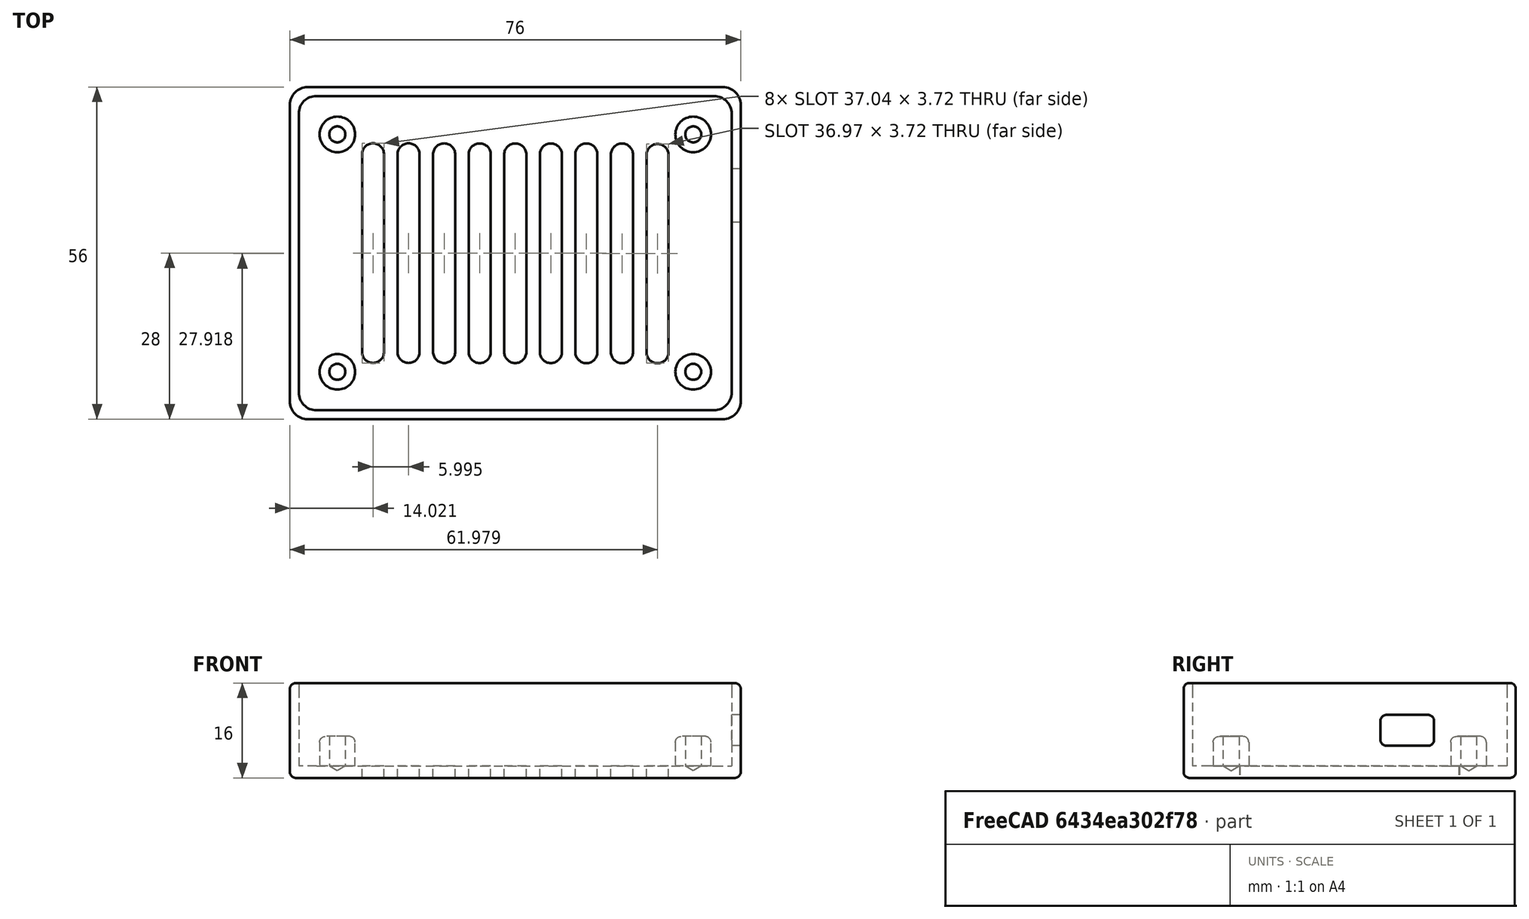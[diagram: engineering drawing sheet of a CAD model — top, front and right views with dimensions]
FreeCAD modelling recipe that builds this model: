
FCSTD DOCUMENT  (FreeCAD 0.19R24267 +99 (Git))
Label: shell_nixie_clock_lite
License: All rights reserved
LicenseURL: http://en.wikipedia.org/wiki/All_rights_reserved
objects: Sketcher::SketchObject×6, PartDesign::Fillet×6, PartDesign::Pad×5, PartDesign::Pocket×4, PartDesign::Hole×1, PartDesign::Body×1, Mesh::Feature×1
note: 39 computed .brp shape members not serialized (recipe doc carries the construction recipe); baked Part::Feature solids carry a one-line shape summary decoded from their .brp

FEATURE [Sketcher::SketchObject] Sketch
  FullyConstrained = false
  MapMode = 5
  Support = -> [XY_Plane]
  sketch-geometry (5):
    g0: LineSegment StartX=-38 StartY=28 StartZ=0 EndX=38 EndY=28 EndZ=0
    g1: LineSegment StartX=38 StartY=28 StartZ=0 EndX=38 EndY=-28 EndZ=0
    g2: LineSegment StartX=38 StartY=-28 StartZ=0 EndX=-38 EndY=-28 EndZ=0
    g3: LineSegment StartX=-38 StartY=-28 StartZ=0 EndX=-38 EndY=28 EndZ=0
    g4: GeomPoint X=-1.52834 Y=31.4249 Z=0
  constraints (10):
    c: Coincident(g0,g1)
    c: Coincident(g1,g2)
    c: Coincident(g2,g3)
    c: Coincident(g3,g0)
    c: Horizontal(g2)
    c: Vertical(g1)
    c: Symmetric(g2,g0,g-1)
    c: Symmetric(g0,g0,g-2)
    c: Distance(g0) = 76
    c: Distance(g3) = 56
FEATURE [PartDesign::Pad] Pad
  Direction = (1,1,1)
  Length = 2
  Length2 = 100
  Profile = -> Sketch
  Type = 0
FEATURE [PartDesign::Fillet] Fillet
  Base = -> Pad [Edge2,Edge5,Edge8,Edge1]
  BaseFeature = -> Pad
  Radius = 3
  SupportTransform = false
FEATURE [PartDesign::Pad] Pad001
  BaseFeature = -> Fillet
  Direction = (1,1,1)
  Length = 14
  Length2 = 100
  Profile = -> Fillet [Face5]
  Type = 0
FEATURE [Sketcher::SketchObject] Sketch001
  FullyConstrained = true
  MapMode = 5
  Placement = pos=(0,0,16) rot=(0,0,1;0rad)
  Support = -> [Pad001]
  sketch-geometry (4):
    g0: LineSegment StartX=-36.5 StartY=26.5 StartZ=0 EndX=36.5 EndY=26.5 EndZ=0
    g1: LineSegment StartX=36.5 StartY=26.5 StartZ=0 EndX=36.5 EndY=-26.5 EndZ=0
    g2: LineSegment StartX=36.5 StartY=-26.5 StartZ=0 EndX=-36.5 EndY=-26.5 EndZ=0
    g3: LineSegment StartX=-36.5 StartY=-26.5 StartZ=0 EndX=-36.5 EndY=26.5 EndZ=0
  constraints (10):
    c: Coincident(g0,g1)
    c: Coincident(g1,g2)
    c: Coincident(g2,g3)
    c: Coincident(g3,g0)
    c: Horizontal(g2)
    c: Vertical(g1)
    c: Symmetric(g2,g0,g-1)
    c: Symmetric(g0,g0,g-2)
    c: Distance(g0) = 73
    c: Distance(g3) = 53
FEATURE [PartDesign::Pocket] Pocket
  BaseFeature = -> Pad001
  Length = 1
  Length2 = 100
  Profile = -> Sketch001
  Type = 0
FEATURE [PartDesign::Pocket] Pocket001
  BaseFeature = -> Pocket
  Length = 14
  Length2 = 100
  Profile = -> Sketch001
  Type = 0
FEATURE [PartDesign::Fillet] Fillet001
  Base = -> Pocket001 [Edge58,Edge56,Edge53,Edge55]
  BaseFeature = -> Pocket001
  Radius = 3
  SupportTransform = false
FEATURE [Sketcher::SketchObject] Sketch002
  FullyConstrained = true
  MapMode = 5
  Placement = pos=(0,0,2) rot=(0,0,1;0rad)
  Support = -> [Fillet001]
  sketch-geometry (12):
    g0: LineSegment StartX=-35 StartY=25 StartZ=0 EndX=35 EndY=25 EndZ=0
    g1: LineSegment StartX=35 StartY=25 StartZ=0 EndX=35 EndY=-25 EndZ=0
    g2: LineSegment StartX=35 StartY=-25 StartZ=0 EndX=-35 EndY=-25 EndZ=0
    g3: LineSegment StartX=-35 StartY=-25 StartZ=0 EndX=-35 EndY=25 EndZ=0
    g4: Circle CenterX=-29.9885 CenterY=20.019 CenterZ=0 NormalX=0 NormalY=0 NormalZ=1 AngleXU=0 Radius=3
    g5: LineSegment StartX=-29.9885 StartY=20.019 StartZ=0 EndX=29.9885 EndY=20.019 EndZ=0
    g6: LineSegment StartX=29.9885 StartY=20.019 StartZ=0 EndX=29.9885 EndY=-20.019 EndZ=0
    g7: LineSegment StartX=29.9885 StartY=-20.019 StartZ=0 EndX=-29.9885 EndY=-20.019 EndZ=0
    g8: LineSegment StartX=-29.9885 StartY=-20.019 StartZ=0 EndX=-29.9885 EndY=20.019 EndZ=0
    g9: Circle CenterX=29.9885 CenterY=20.019 CenterZ=0 NormalX=0 NormalY=0 NormalZ=1 AngleXU=0 Radius=3
    g10: Circle CenterX=-29.9885 CenterY=-20.019 CenterZ=0 NormalX=0 NormalY=0 NormalZ=1 AngleXU=0 Radius=3
    g11: Circle CenterX=29.9885 CenterY=-20.019 CenterZ=0 NormalX=0 NormalY=0 NormalZ=1 AngleXU=0 Radius=3
  constraints (28):
    c: Coincident(g0,g1)
    c: Coincident(g1,g2)
    c: Coincident(g2,g3)
    c: Coincident(g3,g0)
    c: Horizontal(g2)
    c: Vertical(g1)
    c: Symmetric(g0,g2,g-1)
    c: Symmetric(g0,g0,g-2)
    c: Distance(g0) = 70
    c: Distance(g3) = 50
    c: Radius(g4) = 3
    c: Coincident(g5,g6)
    c: Coincident(g6,g7)
    c: Coincident(g7,g8)
    c: Coincident(g8,g5)
    c: Horizontal(g7)
    c: Vertical(g6)
    c: Coincident(g5,g4)
    c: Symmetric(g4,g7,g-1)
    c: Symmetric(g4,g5,g-2)
    c: Distance(g5) = 59.977
    c: Distance(g6) = 40.038
    c: Coincident(g9,g5)
    c: Radius(g9) = 3
    c: Coincident(g10,g7)
    c: Coincident(g11,g6)
    c: Radius(g10) = 3
    c: Radius(g11) = 3
FEATURE [PartDesign::Pad] Pad002
  BaseFeature = -> Fillet001
  Direction = (1,1,1)
  Length = 5
  Length2 = 100
  Profile = -> Sketch002
  Type = 0
FEATURE [PartDesign::Pad] Pad003
  BaseFeature = -> Pad002
  Direction = (1,1,1)
  Length = 5
  Length2 = 100
  Profile = -> Sketch002
  Type = 0
FEATURE [PartDesign::Fillet] Fillet002
  Base = -> Fillet001 [Edge10]
  BaseFeature = -> Fillet001
  Radius = 1
  SupportTransform = false
FEATURE [PartDesign::Pad] Pad004
  BaseFeature = -> Fillet002
  Direction = (1,1,1)
  Length = 5
  Length2 = 100
  Profile = -> Sketch002
  Type = 0
FEATURE [Sketcher::SketchObject] Sketch003
  FullyConstrained = true
  MapMode = 5
  Placement = pos=(0,0,7) rot=(0,0,1;0rad)
  Support = -> [Pad004]
  sketch-geometry (12):
    g0: LineSegment StartX=-29.9985 StartY=20.019 StartZ=0 EndX=29.9985 EndY=20.019 EndZ=0
    g1: LineSegment StartX=29.9985 StartY=20.019 StartZ=0 EndX=29.9985 EndY=-20.019 EndZ=0
    g2: LineSegment StartX=29.9985 StartY=-20.019 StartZ=0 EndX=-29.9985 EndY=-20.019 EndZ=0
    g3: LineSegment StartX=-29.9985 StartY=-20.019 StartZ=0 EndX=-29.9985 EndY=20.019 EndZ=0
    g4: LineSegment StartX=-35 StartY=25 StartZ=0 EndX=35 EndY=25 EndZ=0
    g5: LineSegment StartX=35 StartY=25 StartZ=0 EndX=35 EndY=-25 EndZ=0
    g6: LineSegment StartX=35 StartY=-25 StartZ=0 EndX=-35 EndY=-25 EndZ=0
    g7: LineSegment StartX=-35 StartY=-25 StartZ=0 EndX=-35 EndY=25 EndZ=0
    g8: Circle CenterX=29.9985 CenterY=-20.019 CenterZ=0 NormalX=0 NormalY=0 NormalZ=1 AngleXU=0 Radius=1.5
    g9: Circle CenterX=-29.9985 CenterY=-20.019 CenterZ=0 NormalX=0 NormalY=0 NormalZ=1 AngleXU=0 Radius=1.5
    g10: Circle CenterX=-29.9985 CenterY=20.019 CenterZ=0 NormalX=0 NormalY=0 NormalZ=1 AngleXU=0 Radius=1.5
    g11: Circle CenterX=29.9985 CenterY=20.019 CenterZ=0 NormalX=0 NormalY=0 NormalZ=1 AngleXU=0 Radius=1.5
  constraints (28):
    c: Coincident(g0,g1)
    c: Coincident(g1,g2)
    c: Coincident(g2,g3)
    c: Coincident(g3,g0)
    c: Horizontal(g2)
    c: Vertical(g1)
    c: Symmetric(g0,g2,g-1)
    c: Symmetric(g0,g0,g-2)
    c: Coincident(g4,g5)
    c: Coincident(g5,g6)
    c: Coincident(g6,g7)
    c: Coincident(g7,g4)
    c: Horizontal(g6)
    c: Vertical(g5)
    c: Symmetric(g6,g4,g-1)
    c: Symmetric(g4,g4,g-2)
    c: Distance(g4) = 70
    c: Distance(g7) = 50
    c: Distance(g0) = 59.997
    c: Distance(g1) = 40.038
    c: Coincident(g8,g1)
    c: Coincident(g9,g2)
    c: Coincident(g10,g0)
    c: Coincident(g11,g0)
    c: Radius(g11) = 1.5
    c: Radius(g8) = 1.5
    c: Radius(g9) = 1.5
    c: Radius(g10) = 1.5
FEATURE [PartDesign::Hole] Hole001
  BaseFeature = -> Pad004
  Depth = 5
  DepthType = 0
  Diameter = 2.7
  DrillForDepth = false
  DrillPoint = 1
  DrillPointAngle = 118
  HoleCutCountersinkAngle = 90
  HoleCutCustomValues = false
  HoleCutDepth = 0
  HoleCutDiameter = 6.1
  HoleCutType = 0
  ModelActualThread = false
  Profile = -> Sketch003
  Tapered = false
  TaperedAngle = 90
  ThreadAngle = 0
  ThreadClass = 0
  ThreadCutOffInner = 0
  ThreadCutOffOuter = 0
  ThreadDirection = 0
  ThreadFit = 0
  ThreadPitch = 0
  ThreadSize = 0
  ThreadType = 0
  Threaded = false
FEATURE [PartDesign::Fillet] Fillet003
  Base = -> Hole001 [Edge88]
  BaseFeature = -> Hole001
  Radius = 1
  SupportTransform = false
FEATURE [Sketcher::SketchObject] Sketch004
  FullyConstrained = false
  MapMode = 5
  Placement = pos=(38,0,0) rot=(0.57735,0.57735,0.57735;2.0944rad)
  Support = -> [Fillet003]
  sketch-geometry (8):
    g0: LineSegment StartX=-25 StartY=14.3199 StartZ=0 EndX=25 EndY=14.3199 EndZ=0
    g1: LineSegment StartX=25 StartY=14.3199 StartZ=0 EndX=25 EndY=5.31988 EndZ=0
    g2: LineSegment StartX=25 StartY=5.31988 StartZ=0 EndX=-25 EndY=5.31988 EndZ=0
    g3: LineSegment StartX=-25 StartY=5.31988 StartZ=0 EndX=-25 EndY=14.3199 EndZ=0
    g4: LineSegment StartX=5.187 StartY=10.6199 StartZ=0 EndX=14.205 EndY=10.6199 EndZ=0
    g5: LineSegment StartX=14.205 StartY=10.6199 StartZ=0 EndX=14.205 EndY=5.41988 EndZ=0
    g6: LineSegment StartX=14.205 StartY=5.41988 StartZ=0 EndX=5.187 EndY=5.41988 EndZ=0
    g7: LineSegment StartX=5.187 StartY=5.41988 StartZ=0 EndX=5.187 EndY=10.6199 EndZ=0
  constraints (22):
    c: Coincident(g0,g1)
    c: Coincident(g1,g2)
    c: Coincident(g2,g3)
    c: Coincident(g3,g0)
    c: Horizontal(g2)
    c: Vertical(g1)
    c: Vertical(g3)
    c: Symmetric(g0,g0,g-2)
    c: Distance(g0) = 50
    c: Distance(g3) = 9
    c: Coincident(g4,g5)
    c: Coincident(g5,g6)
    c: Coincident(g6,g7)
    c: Coincident(g7,g4)
    c: Horizontal(g4)
    c: Horizontal(g6)
    c: Vertical(g5)
    c: Vertical(g7)
    c: Distance(g4) = 9.018
    c: Distance(g5) = 5.2
    c: Distance(g5,g1) = 10.795
    c: Distance(g5,g2) = 0.1
FEATURE [PartDesign::Pocket] Pocket002
  BaseFeature = -> Fillet003
  Length = 3
  Length2 = 100
  Profile = -> Sketch004
  Type = 0
FEATURE [PartDesign::Fillet] Fillet004
  Base = -> Pocket002 [Edge101,Edge107,Edge105,Edge103]
  BaseFeature = -> Pocket002
  Radius = 1
  SupportTransform = false
FEATURE [PartDesign::Fillet] Fillet005
  Base = -> Fillet004 [Edge132,Edge134,Edge138,Edge136]
  BaseFeature = -> Fillet004
  Radius = 1
  SupportTransform = false
FEATURE [Sketcher::SketchObject] Sketch005
  FullyConstrained = true
  MapMode = 5
  Placement = pos=(0,0,0) rot=(1,0,0;3.14159rad)
  Support = -> [Fillet005]
  sketch-geometry (52):
    g0: LineSegment StartX=-29.9885 StartY=20.019 StartZ=0 EndX=29.9885 EndY=20.019 EndZ=0
    g1: LineSegment StartX=29.9885 StartY=20.019 StartZ=0 EndX=29.9885 EndY=-20.019 EndZ=0
    g2: LineSegment StartX=29.9885 StartY=-20.019 StartZ=0 EndX=-29.9885 EndY=-20.019 EndZ=0
    g3: LineSegment StartX=-29.9885 StartY=-20.019 StartZ=0 EndX=-29.9885 EndY=20.019 EndZ=0
    g4: LineSegment StartX=-28.4885 StartY=18.519 StartZ=0 EndX=28.4885 EndY=18.519 EndZ=0
    g5: LineSegment StartX=28.4885 StartY=18.519 StartZ=0 EndX=28.4885 EndY=-18.519 EndZ=0
    g6: LineSegment StartX=28.4885 StartY=-18.519 StartZ=0 EndX=-28.4885 EndY=-18.519 EndZ=0
    g7: LineSegment StartX=-28.4885 StartY=-18.519 StartZ=0 EndX=-28.4885 EndY=18.519 EndZ=0
    g8: ArcOfCircle CenterX=-23.9785 CenterY=16.659 CenterZ=0 NormalX=0 NormalY=0 NormalZ=1 AngleXU=0 Radius=1.86 StartAngle=-9e-16 EndAngle=3.14159
    g9: ArcOfCircle CenterX=-23.9785 CenterY=-16.659 CenterZ=0 NormalX=0 NormalY=0 NormalZ=1 AngleXU=0 Radius=1.86 StartAngle=3.14159 EndAngle=6.28319
    g10: LineSegment StartX=-25.8385 StartY=16.659 StartZ=0 EndX=-25.8385 EndY=-16.659 EndZ=0
    g11: LineSegment StartX=-22.1185 StartY=16.659 StartZ=0 EndX=-22.1185 EndY=-16.659 EndZ=0
    g12: ArcOfCircle CenterX=-17.9839 CenterY=16.665 CenterZ=0 NormalX=0 NormalY=0 NormalZ=1 AngleXU=0 Radius=1.86 StartAngle=-9e-16 EndAngle=3.14159
    g13: ArcOfCircle CenterX=-17.9839 CenterY=-16.655 CenterZ=0 NormalX=0 NormalY=0 NormalZ=1 AngleXU=0 Radius=1.86 StartAngle=3.14159 EndAngle=6.28319
    g14: LineSegment StartX=-19.8439 StartY=16.665 StartZ=0 EndX=-19.8439 EndY=-16.655 EndZ=0
    g15: LineSegment StartX=-16.1239 StartY=16.665 StartZ=0 EndX=-16.1239 EndY=-16.655 EndZ=0
    g16: LineSegment StartX=-22.1185 StartY=16.659 StartZ=0 EndX=-16.1239 EndY=16.665 EndZ=0
    g17: ArcOfCircle CenterX=-11.9892 CenterY=16.671 CenterZ=0 NormalX=0 NormalY=0 NormalZ=1 AngleXU=0 Radius=1.86 StartAngle=-9e-16 EndAngle=3.14159
    g18: ArcOfCircle CenterX=-11.9892 CenterY=-16.649 CenterZ=0 NormalX=0 NormalY=0 NormalZ=1 AngleXU=0 Radius=1.86 StartAngle=3.14159 EndAngle=6.28319
    g19: LineSegment StartX=-13.8492 StartY=16.671 StartZ=0 EndX=-13.8492 EndY=-16.649 EndZ=0
    g20: LineSegment StartX=-10.1292 StartY=16.671 StartZ=0 EndX=-10.1292 EndY=-16.649 EndZ=0
    g21: LineSegment StartX=-16.1239 StartY=16.665 StartZ=0 EndX=-10.1292 EndY=16.671 EndZ=0
    g22: ArcOfCircle CenterX=-5.9946 CenterY=16.6771 CenterZ=0 NormalX=0 NormalY=0 NormalZ=1 AngleXU=0 Radius=1.86 StartAngle=-9e-16 EndAngle=3.14159
    g23: ArcOfCircle CenterX=-5.9946 CenterY=-16.6429 CenterZ=0 NormalX=0 NormalY=0 NormalZ=1 AngleXU=0 Radius=1.86 StartAngle=3.14159 EndAngle=6.28319
    g24: LineSegment StartX=-7.8546 StartY=16.6771 StartZ=0 EndX=-7.8546 EndY=-16.6429 EndZ=0
    g25: LineSegment StartX=-4.1346 StartY=16.6771 StartZ=0 EndX=-4.1346 EndY=-16.6429 EndZ=0
    g26: LineSegment StartX=-10.1292 StartY=16.671 StartZ=0 EndX=-4.1346 EndY=16.6771 EndZ=0
    g27: ArcOfCircle CenterX=3.6e-05 CenterY=16.6831 CenterZ=0 NormalX=0 NormalY=0 NormalZ=1 AngleXU=0 Radius=1.86 StartAngle=-9e-16 EndAngle=3.14159
    g28: ArcOfCircle CenterX=3.6e-05 CenterY=-16.6369 CenterZ=0 NormalX=0 NormalY=0 NormalZ=1 AngleXU=0 Radius=1.86 StartAngle=3.14159 EndAngle=6.28319
    g29: LineSegment StartX=-1.85996 StartY=16.6831 StartZ=0 EndX=-1.85996 EndY=-16.6369 EndZ=0
    g30: LineSegment StartX=1.86004 StartY=16.6831 StartZ=0 EndX=1.86004 EndY=-16.6369 EndZ=0
    g31: LineSegment StartX=-4.1346 StartY=16.6771 StartZ=0 EndX=1.86004 EndY=16.6831 EndZ=0
    g32: ArcOfCircle CenterX=5.99467 CenterY=16.6891 CenterZ=0 NormalX=0 NormalY=0 NormalZ=1 AngleXU=0 Radius=1.86 StartAngle=-9e-16 EndAngle=3.14159
    g33: ArcOfCircle CenterX=5.99467 CenterY=-16.6309 CenterZ=0 NormalX=0 NormalY=0 NormalZ=1 AngleXU=0 Radius=1.86 StartAngle=3.14159 EndAngle=6.28319
    g34: LineSegment StartX=4.13467 StartY=16.6891 StartZ=0 EndX=4.13467 EndY=-16.6309 EndZ=0
    g35: LineSegment StartX=7.85467 StartY=16.6891 StartZ=0 EndX=7.85467 EndY=-16.6309 EndZ=0
    g36: LineSegment StartX=1.86004 StartY=16.6831 StartZ=0 EndX=7.85467 EndY=16.6891 EndZ=0
    g37: ArcOfCircle CenterX=11.9893 CenterY=16.6951 CenterZ=0 NormalX=0 NormalY=0 NormalZ=1 AngleXU=0 Radius=1.86 StartAngle=-9e-16 EndAngle=3.14159
    g38: ArcOfCircle CenterX=11.9893 CenterY=-16.6249 CenterZ=0 NormalX=0 NormalY=0 NormalZ=1 AngleXU=0 Radius=1.86 StartAngle=3.14159 EndAngle=6.28319
    g39: LineSegment StartX=10.1293 StartY=16.6951 StartZ=0 EndX=10.1293 EndY=-16.6249 EndZ=0
    g40: LineSegment StartX=13.8493 StartY=16.6951 StartZ=0 EndX=13.8493 EndY=-16.6249 EndZ=0
    g41: LineSegment StartX=7.85467 StartY=16.6891 StartZ=0 EndX=13.8493 EndY=16.6951 EndZ=0
    g42: ArcOfCircle CenterX=17.9839 CenterY=16.7012 CenterZ=0 NormalX=0 NormalY=0 NormalZ=1 AngleXU=0 Radius=1.86 StartAngle=-9e-16 EndAngle=3.14159
    g43: ArcOfCircle CenterX=17.9839 CenterY=-16.6188 CenterZ=0 NormalX=0 NormalY=0 NormalZ=1 AngleXU=0 Radius=1.86 StartAngle=3.14159 EndAngle=6.28319
    g44: LineSegment StartX=16.1239 StartY=16.7012 StartZ=0 EndX=16.1239 EndY=-16.6188 EndZ=0
    g45: LineSegment StartX=19.8439 StartY=16.7012 StartZ=0 EndX=19.8439 EndY=-16.6188 EndZ=0
    g46: LineSegment StartX=13.8493 StartY=16.6951 StartZ=0 EndX=19.8439 EndY=16.7012 EndZ=0
    g47: ArcOfCircle CenterX=23.9786 CenterY=16.7072 CenterZ=0 NormalX=0 NormalY=0 NormalZ=1 AngleXU=0 Radius=1.86 StartAngle=-9e-16 EndAngle=3.14159
    g48: ArcOfCircle CenterX=23.9786 CenterY=-16.5428 CenterZ=0 NormalX=0 NormalY=0 NormalZ=1 AngleXU=0 Radius=1.86 StartAngle=3.14159 EndAngle=6.28319
    g49: LineSegment StartX=22.1186 StartY=16.7072 StartZ=0 EndX=22.1186 EndY=-16.5428 EndZ=0
    g50: LineSegment StartX=25.8386 StartY=16.7072 StartZ=0 EndX=25.8386 EndY=-16.5428 EndZ=0
    g51: LineSegment StartX=19.8439 StartY=16.7012 StartZ=0 EndX=25.8386 EndY=16.7072 EndZ=0
  constraints (126):
    c: Coincident(g0,g1)
    c: Coincident(g1,g2)
    c: Coincident(g2,g3)
    c: Coincident(g3,g0)
    c: Horizontal(g2)
    c: Vertical(g1)
    c: Symmetric(g2,g0,g-1)
    c: Symmetric(g0,g0,g-2)
    c: Distance(g0) = 59.977
    c: Distance(g1) = 40.038
    c: Coincident(g4,g5)
    c: Coincident(g5,g6)
    c: Coincident(g6,g7)
    c: Coincident(g7,g4)
    c: Horizontal(g6)
    c: Vertical(g5)
    c: Symmetric(g4,g6,g-1)
    c: Symmetric(g4,g4,g-2)
    c: Distance(g4) = 56.977
    c: Distance(g5) = 37.038
    c: Tangent(g8,g11) = 1.5708
    c: Tangent(g8,g10) = -1.5708
    c: Tangent(g10,g9) = -1.5708
    c: Tangent(g11,g9) = 1.5708
    c: Vertical(g10)
    c: Equal(g8,g9)
    c: Tangent(g8,g4)
    c: Tangent(g9,g6)
    c: Tangent(g12,g15) = 1.5708
    c: Tangent(g12,g14) = -1.5708
    c: Tangent(g14,g13) = -1.5708
    c: Tangent(g15,g13) = 1.5708
    c: Vertical(g14)
    c: Equal(g12,g13)
    c: Coincident(g8,g16)
    c: Coincident(g12,g16)
    c: Distance(g16) = 5.99464
    c: Angle(g16) = 0.00100456
    c: Tangent(g17,g20) = 1.5708
    c: Tangent(g17,g19) = -1.5708
    c: Tangent(g19,g18) = -1.5708
    c: Tangent(g20,g18) = 1.5708
    c: Vertical(g19)
    c: Equal(g17,g18)
    c: Coincident(g12,g21)
    c: Coincident(g17,g21)
    c: Equal(g16,g21)
    c: Parallel(g21,g16)
    c: Tangent(g22,g25) = 1.5708
    c: Tangent(g22,g24) = -1.5708
    c: Tangent(g24,g23) = -1.5708
    c: Tangent(g25,g23) = 1.5708
    c: Vertical(g24)
    c: Equal(g22,g23)
    c: Coincident(g17,g26)
    c: Coincident(g22,g26)
    c: Equal(g16,g26)
    c: Parallel(g26,g16)
    c: Tangent(g27,g30) = 1.5708
    c: Tangent(g27,g29) = -1.5708
    c: Tangent(g29,g28) = -1.5708
    c: Tangent(g30,g28) = 1.5708
    c: Vertical(g29)
    c: Equal(g27,g28)
    c: Coincident(g22,g31)
    c: Coincident(g27,g31)
    c: Equal(g16,g31)
    c: Parallel(g31,g16)
    c: Tangent(g32,g35) = 1.5708
    c: Tangent(g32,g34) = -1.5708
    c: Tangent(g34,g33) = -1.5708
    c: Tangent(g35,g33) = 1.5708
    c: Vertical(g34)
    c: Equal(g32,g33)
    c: Coincident(g27,g36)
    c: Coincident(g32,g36)
    c: Equal(g16,g36)
    c: Parallel(g36,g16)
    c: Tangent(g37,g40) = 1.5708
    c: Tangent(g37,g39) = -1.5708
    c: Tangent(g39,g38) = -1.5708
    c: Tangent(g40,g38) = 1.5708
    c: Vertical(g39)
    c: Equal(g37,g38)
    c: Coincident(g32,g41)
    c: Coincident(g37,g41)
    c: Equal(g16,g41)
    c: Parallel(g41,g16)
    c: Tangent(g42,g45) = 1.5708
    c: Tangent(g42,g44) = -1.5708
    c: Tangent(g44,g43) = -1.5708
    c: Tangent(g45,g43) = 1.5708
    c: Vertical(g44)
    c: Equal(g42,g43)
    c: Coincident(g37,g46)
    c: Coincident(g42,g46)
    c: Equal(g16,g46)
    c: Parallel(g46,g16)
    c: Tangent(g47,g50) = 1.5708
    c: Tangent(g47,g49) = -1.5708
    c: Tangent(g49,g48) = -1.5708
    c: Tangent(g50,g48) = 1.5708
    c: Vertical(g49)
    c: Equal(g47,g48)
    c: Coincident(g42,g51)
    c: Coincident(g47,g51)
    c: Equal(g16,g51)
    c: Parallel(g51,g16)
    c: Radius(g47) = 1.86
    c: Equal(g12,g8)
    c: Equal(g12,g17)
    c: Equal(g12,g22)
    c: Equal(g12,g27)
    c: Equal(g12,g32)
    c: Equal(g12,g37)
    c: Equal(g12,g42)
    c: Radius(g12) = 1.86
    c: Distance(g8,g7) = 2.65
    c: Distance(g14) = 33.32
    c: Distance(g19) = 33.32
    c: Distance(g24) = 33.32
    c: Distance(g29) = 33.32
    c: Distance(g34) = 33.32
    c: Distance(g39) = 33.32
    c: Distance(g44) = 33.32
    c: Distance(g49) = 33.25
FEATURE [PartDesign::Pocket] Pocket003
  BaseFeature = -> Fillet005
  Length = 2
  Length2 = 100
  Profile = -> Sketch005
  Type = 0
FEATURE [PartDesign::Body] Body  label="外壳"
  Group = -> [Sketch,Pad,Fillet,Pad001,Sketch001,Pocket,Pocket001,Fillet001,Sketch002,Pad002,Sketch003,Pad003,Fillet002,Pad004,Hole001,Fillet003,Sketch004,Pocket002,Fillet004,Fillet005,Sketch005,Pocket003]
  Origin = -> Origin
  Tip = -> Pocket003
FEATURE [Mesh::Feature] Mesh  label="外壳 (Meshed)"
  Placement = pos=(82,0,0) rot=(0,0,1;0rad)
